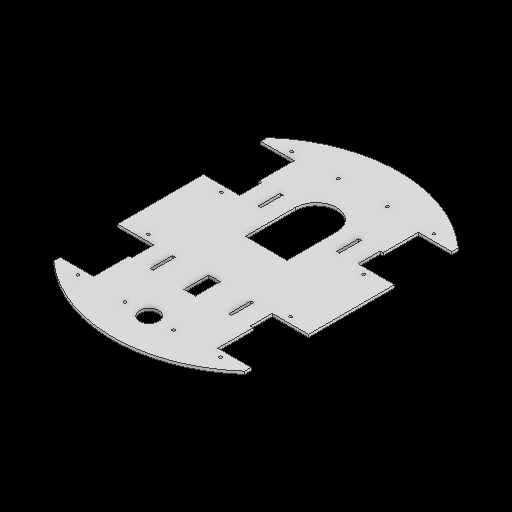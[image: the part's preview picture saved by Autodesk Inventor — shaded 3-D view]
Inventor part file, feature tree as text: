
AUTODESK INVENTOR PART (.ipt)
format: ipt  version: 2025.2 (Build 292293000, 293)  size: 177,152 bytes
history: native  units: in
note: dims shown in document units (in); Inventor stores cm internally (conversion verified against a paired STEP export)
features: extrude x1, sketch x1
ambient origin geometry x8: Origin, YZ Plane, XZ Plane, XY Plane, X Axis, Y Axis, Z Axis, Center Point
bodies: Solid1 (feature_tree)
feature tree (2):
  extrude  "Extrusion1"  [1 undecoded]
  sketch  "Sketch1"  dims[d0=0.1181in d1=0.0in]
note: 1 required parameter value undecoded (feature->parameter linkage not recoverable at this tier; creation-order binding heuristic only, values carry confidence <= 0.55)
